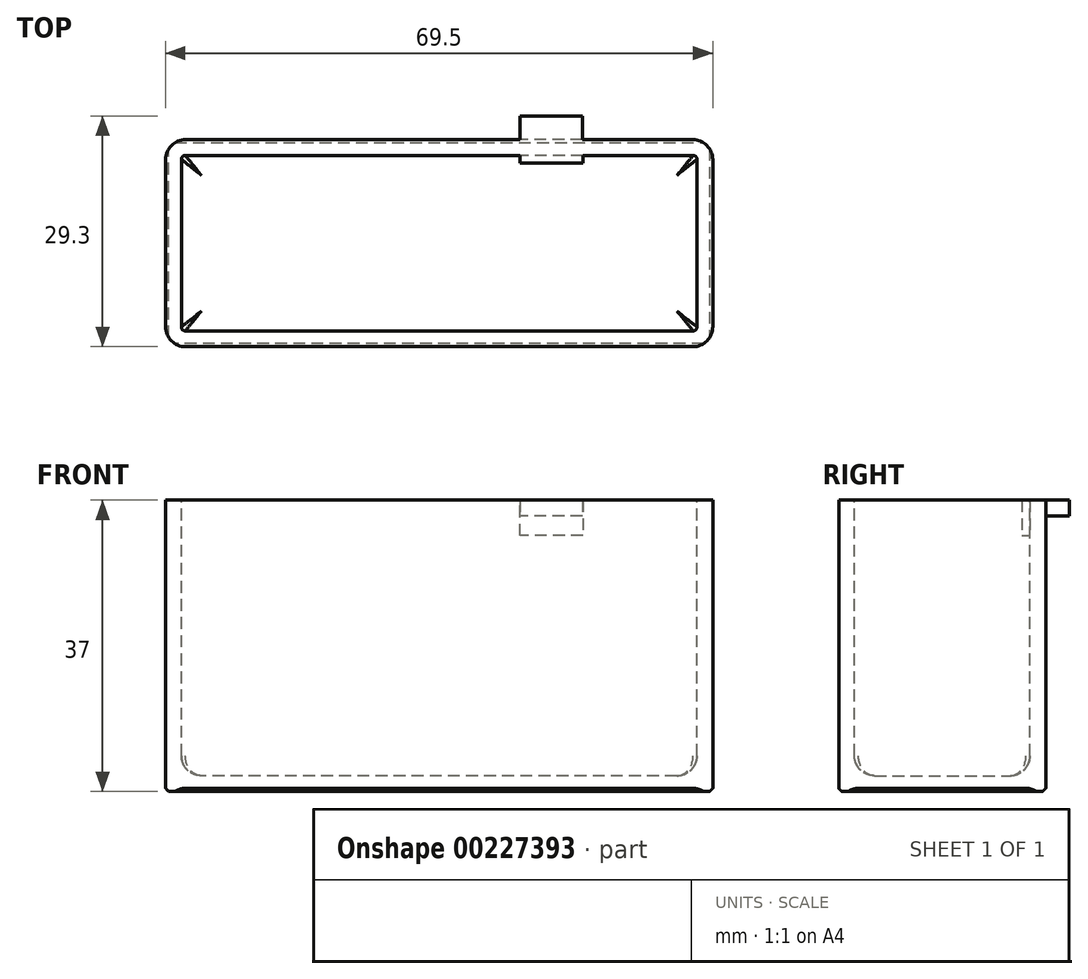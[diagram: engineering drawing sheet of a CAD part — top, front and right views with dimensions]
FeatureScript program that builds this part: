
annotation { "Feature Type Name" : "Feature", "Feature Type Description" : "" }
export const myFeature = defineFeature(function(context is Context, id is Id, definition is map)
    precondition{}
    {
        {
            var Q0;
            Q0=qCreatedBy(makeId("Top.planeOp"),FACE);
            var sketch = newSketch(context, id + "F0", { "sketchPlane" : qUnion([Q0])});
            skLineSegment(sketch, "E0.bottom", {"start": v(34.75, -13.15) * mm, "end": v(-34.75, -13.15) * mm});
            skLineSegment(sketch, "E0.top", {"start": v(34.75, 13.15) * mm, "end": v(-34.75, 13.15) * mm});
            skLineSegment(sketch, "E0.left", {"start": v(34.75, -13.15) * mm, "end": v(34.75, 13.15) * mm});
            skLineSegment(sketch, "E0.right", {"start": v(-34.75, -13.15) * mm, "end": v(-34.75, 13.15) * mm});
            skPoint(sketch, "E0.middle", {"position": v(0, 0) * mm});
            skSolve(sketch);
        }
        {
            var Q0;
            Q0 = qSketchRegion(id + "F0", true);
            extrude(context, id + "F1", {"entities" : qUnion([Q0]), "depth" : 37 * mm});
        }
        {
            var Q0;
            Q0=makeQuery(id+"F1.opExtrude","CAP_FACE",FACE,{"disambiguationData":[OSD([sQuery(id+"F0.wireOp",EDGE,"E0.bottom"),sQuery(id+"F0.wireOp",EDGE,"E0.top"),sQuery(id+"F0.wireOp",EDGE,"E0.left"),sQuery(id+"F0.wireOp",EDGE,"E0.right")])],"isStart":false});
            var sketch = newSketch(context, id + "F2", { "sketchPlane" : qUnion([Q0])});
            skLineSegment(sketch, "E1.bottom", {"start": v(32.75, -11.15) * mm, "end": v(-32.75, -11.15) * mm});
            skLineSegment(sketch, "E1.top", {"start": v(32.75, 11.15) * mm, "end": v(-32.75, 11.15) * mm});
            skLineSegment(sketch, "E1.left", {"start": v(32.75, -11.15) * mm, "end": v(32.75, 11.15) * mm});
            skLineSegment(sketch, "E1.right", {"start": v(-32.75, -11.15) * mm, "end": v(-32.75, 11.15) * mm});
            skPoint(sketch, "E1.middle", {"position": v(0, 0) * mm});
            skSolve(sketch);
        }
        {
            var Q0;
            Q0 = qSketchRegion(id + "F2", true);
            extrude(context, id + "F3", {"entities" : qUnion([Q0]), "operationType" : NewBodyOperationType.REMOVE, "oppositeDirection" : true, "depth" : 35 * mm});
        }
        {
            var Q0;
            Q0=makeQuery(id+"F1.opExtrude","CAP_EDGE",EDGE,{"disambiguationData":[OSD([sQuery(id+"F0.wireOp",EDGE,"E0.bottom")])],"isStart":true});
            var Q1;
            Q1=makeQuery(id+"F1.opExtrude","CAP_EDGE",EDGE,{"disambiguationData":[OSD([sQuery(id+"F0.wireOp",EDGE,"E0.left")])],"isStart":true});
            var Q2;
            Q2=makeQuery(id+"F1.opExtrude","CAP_EDGE",EDGE,{"disambiguationData":[OSD([sQuery(id+"F0.wireOp",EDGE,"E0.top")])],"isStart":true});
            var Q3;
            Q3=makeQuery(id+"F1.opExtrude","CAP_EDGE",EDGE,{"disambiguationData":[OSD([sQuery(id+"F0.wireOp",EDGE,"E0.right")])],"isStart":true});
            chamfer(context, id + "F4", {"entities" : qUnion([Q0, Q1, Q2, Q3]), "width" : .4 * mm, "tangentPropagation" : true});
        }
        {
            var Q0;
            Q0=makeQuery(id+"F1.opExtrude","SWEPT_EDGE",EDGE,{"disambiguationData":[OSD([sQuery(id+"F0.wireOp",EDGE,"E0.top"),sQuery(id+"F0.wireOp",EDGE,"E0.left")])]});
            var Q1;
            Q1=makeQuery(id+"F1.opExtrude","SWEPT_EDGE",EDGE,{"disambiguationData":[OSD([sQuery(id+"F0.wireOp",EDGE,"E0.bottom"),sQuery(id+"F0.wireOp",EDGE,"E0.left")])]});
            var Q2;
            Q2=makeQuery(id+"F1.opExtrude","SWEPT_EDGE",EDGE,{"disambiguationData":[OSD([sQuery(id+"F0.wireOp",EDGE,"E0.top"),sQuery(id+"F0.wireOp",EDGE,"E0.right")])]});
            var Q3;
            Q3=makeQuery(id+"F1.opExtrude","SWEPT_EDGE",EDGE,{"disambiguationData":[OSD([sQuery(id+"F0.wireOp",EDGE,"E0.bottom"),sQuery(id+"F0.wireOp",EDGE,"E0.right")])]});
            fillet(context, id + "F5", {"entities" : qUnion([Q0, Q1, Q2, Q3]), "radius" : 2.54 * mm, "tangentPropagation" : true, "allowEdgeOverflow" : false});
        }
        {
            var Q0;
            Q0=makeQuery(id+"F3.boolean.opBoolean","COPY",EDGE,{"derivedFrom":makeQuery(id+"F3.opExtrude","CAP_EDGE",EDGE,{"disambiguationData":[OSD([sQuery(id+"F2.wireOp",EDGE,"E1.bottom")])],"isStart":false})});
            var Q1;
            Q1=makeQuery(id+"F3.boolean.opBoolean","COPY",EDGE,{"derivedFrom":makeQuery(id+"F3.opExtrude","CAP_EDGE",EDGE,{"disambiguationData":[OSD([sQuery(id+"F2.wireOp",EDGE,"E1.right")])],"isStart":false})});
            var Q2;
            Q2=makeQuery(id+"F3.boolean.opBoolean","COPY",EDGE,{"derivedFrom":makeQuery(id+"F3.opExtrude","CAP_EDGE",EDGE,{"disambiguationData":[OSD([sQuery(id+"F2.wireOp",EDGE,"E1.left")])],"isStart":false})});
            var Q3;
            Q3=makeQuery(id+"F3.boolean.opBoolean","COPY",EDGE,{"derivedFrom":makeQuery(id+"F3.opExtrude","CAP_EDGE",EDGE,{"disambiguationData":[OSD([sQuery(id+"F2.wireOp",EDGE,"E1.top")])],"isStart":false})});
            fillet(context, id + "F6", {"entities" : qUnion([Q0, Q1, Q2, Q3]), "radius" : 2.54 * mm, "tangentPropagation" : true, "allowEdgeOverflow" : false});
        }
        {
            var Q0;
            Q0=makeQuery(id+"F3.boolean.opBoolean","COPY",FACE,{"derivedFrom":makeQuery(id+"F3.opExtrude","SWEPT_FACE",FACE,{"disambiguationData":[OSD([sQuery(id+"F2.wireOp",EDGE,"E1.top")])]})});
            var sketch = newSketch(context, id + "F7", { "sketchPlane" : qUnion([Q0])});
            skLineSegment(sketch, "E2", {"start": v(32.75, 37) * mm, "end": v(18.25, 37) * mm});
            skLineSegment(sketch, "E3", {"start": v(18.25, 37) * mm, "end": v(18.25, 32.5) * mm});
            skLineSegment(sketch, "E4.bottom", {"start": v(18.25, 32.5) * mm, "end": v(10.25, 32.5) * mm});
            skLineSegment(sketch, "E4.top", {"start": v(18.25, 37) * mm, "end": v(10.25, 37) * mm});
            skLineSegment(sketch, "E4.left", {"start": v(18.25, 32.5) * mm, "end": v(18.25, 37) * mm});
            skLineSegment(sketch, "E4.right", {"start": v(10.25, 32.5) * mm, "end": v(10.25, 37) * mm});
            skSolve(sketch);
        }
        {
            var Q0;
            Q0 = qSketchRegion(id + "F7", true);
            extrude(context, id + "F8", {"entities" : qUnion([Q0]), "operationType" : NewBodyOperationType.ADD, "depth" : 1 * mm});
        }
        {
            var Q0;
            Q0=makeQuery(id+"F1.opExtrude","SWEPT_FACE",FACE,{"disambiguationData":[OSD([sQuery(id+"F0.wireOp",EDGE,"E0.top")])]});
            var sketch = newSketch(context, id + "F9", { "sketchPlane" : qUnion([Q0])});
            skLineSegment(sketch, "E5.bottom", {"start": v(-18.19, 37) * mm, "end": v(-10.25, 37) * mm});
            skLineSegment(sketch, "E5.top", {"start": v(-18.19, 35) * mm, "end": v(-10.25, 35) * mm});
            skLineSegment(sketch, "E5.left", {"start": v(-18.19, 37) * mm, "end": v(-18.19, 35) * mm});
            skLineSegment(sketch, "E5.right", {"start": v(-10.25, 37) * mm, "end": v(-10.25, 35) * mm});
            skSolve(sketch);
        }
        {
            var Q0;
            Q0 = qSketchRegion(id + "F9", true);
            extrude(context, id + "F10", {"entities" : qUnion([Q0]), "operationType" : NewBodyOperationType.ADD, "depth" : 3 * mm});
        }
        {
            var Q0;
            Q0=makeQuery(id+"F3.boolean.opBoolean","COPY",EDGE,{"derivedFrom":makeQuery(id+"F3.opExtrude","SWEPT_EDGE",EDGE,{"disambiguationData":[OSD([sQuery(id+"F2.wireOp",EDGE,"E1.top"),sQuery(id+"F2.wireOp",EDGE,"E1.left")])]})});
            var Q1;
            Q1=makeQuery(id+"F3.boolean.opBoolean","COPY",EDGE,{"derivedFrom":makeQuery(id+"F3.opExtrude","SWEPT_EDGE",EDGE,{"disambiguationData":[OSD([sQuery(id+"F2.wireOp",EDGE,"E1.bottom"),sQuery(id+"F2.wireOp",EDGE,"E1.left")])]})});
            var Q2;
            Q2=makeQuery(id+"F3.boolean.opBoolean","COPY",EDGE,{"derivedFrom":makeQuery(id+"F3.opExtrude","SWEPT_EDGE",EDGE,{"disambiguationData":[OSD([sQuery(id+"F2.wireOp",EDGE,"E1.bottom"),sQuery(id+"F2.wireOp",EDGE,"E1.right")])]})});
            var Q3;
            Q3=makeQuery(id+"F3.boolean.opBoolean","COPY",EDGE,{"derivedFrom":makeQuery(id+"F3.opExtrude","SWEPT_EDGE",EDGE,{"disambiguationData":[OSD([sQuery(id+"F2.wireOp",EDGE,"E1.top"),sQuery(id+"F2.wireOp",EDGE,"E1.right")])]})});
            fillet(context, id + "F11", {"entities" : qUnion([Q0, Q1, Q2, Q3]), "radius" : .5 * mm, "tangentPropagation" : true, "allowEdgeOverflow" : false});
        }
    });
